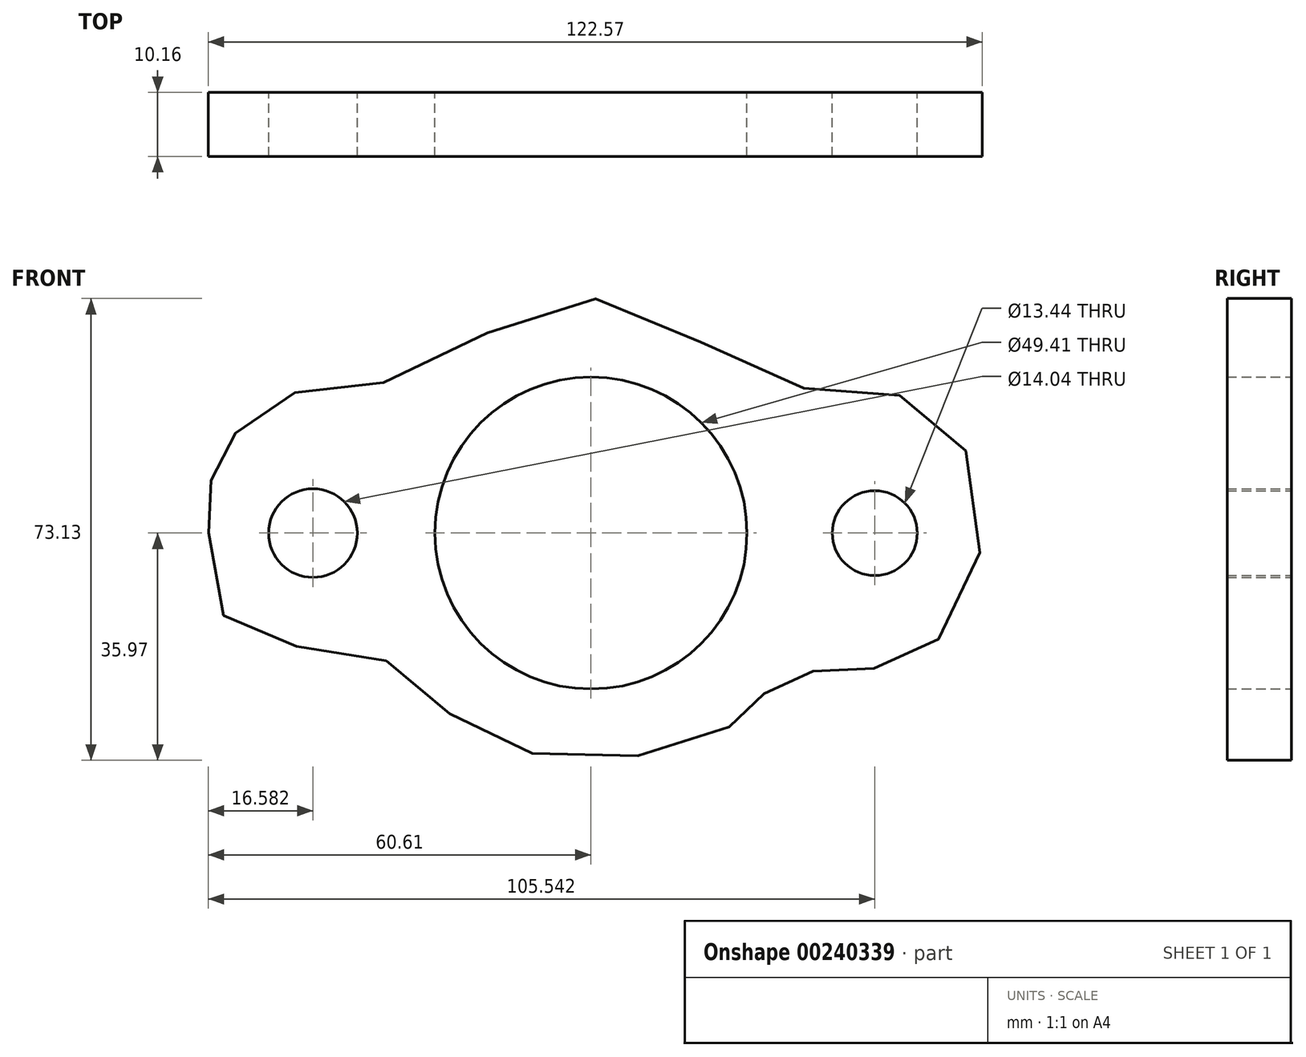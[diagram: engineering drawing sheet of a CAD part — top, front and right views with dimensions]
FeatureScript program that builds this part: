
annotation { "Feature Type Name" : "Feature", "Feature Type Description" : "" }
export const myFeature = defineFeature(function(context is Context, id is Id, definition is map)
    precondition{}
    {
        {
            var Q0;
            Q0=qCreatedBy(makeId("Front.planeOp"),FACE);
            var sketch = newSketch(context, id + "F0", { "sketchPlane" : qUnion([Q0])});
            skCircle(sketch, "E0", {"center": v(0, 0) * mm, "radius": 24.7 * mm});
            skFitSpline(sketch, "E1", {"points": [v(-60.56, 0) * mm, v(-60.3, 7.5) * mm, v(-58.5, 12.39) * mm, v(-50.13, 21.29) * mm, v(-31.2, 24.33) * mm, v(0, 37.16) * mm, v(30.25, 23.76) * mm, v(52.77, 20.43) * mm, v(61.93, 0) * mm, v(52.16, -19.26) * mm, v(40.97, -21.55) * mm, v(32.64, -22.51) * mm, v(26.67, -26.13) * mm, v(22.96, -30.01) * mm, v(0, -35.97) * mm, v(-21.8, -29.04) * mm, v(-35.71, -18.9) * mm, v(-55.91, -15.75) * mm, v(-60.56, 0) * mm]});
            skCircle(sketch, "E2", {"center": v(44.93, 0) * mm, "radius": 6.72 * mm});
            skCircle(sketch, "E3", {"center": v(-44.03, 0) * mm, "radius": 7.02 * mm});
            skSolve(sketch);
        }
        {
            var Q0;
            Q0=makeQuery(id+"F0.imprint","IMPRINT",FACE,{"disambiguationData":[TD([[makeQuery(id+"F0.imprint","IMPRINT",EDGE,{"derivedFrom":sQuery(id+"F0.wireOp",EDGE,"E0")}),-1.0]])]});
            extrude(context, id + "F1", {"entities" : qUnion([Q0]), "depth" : 10.16 * mm});
        }
    });
